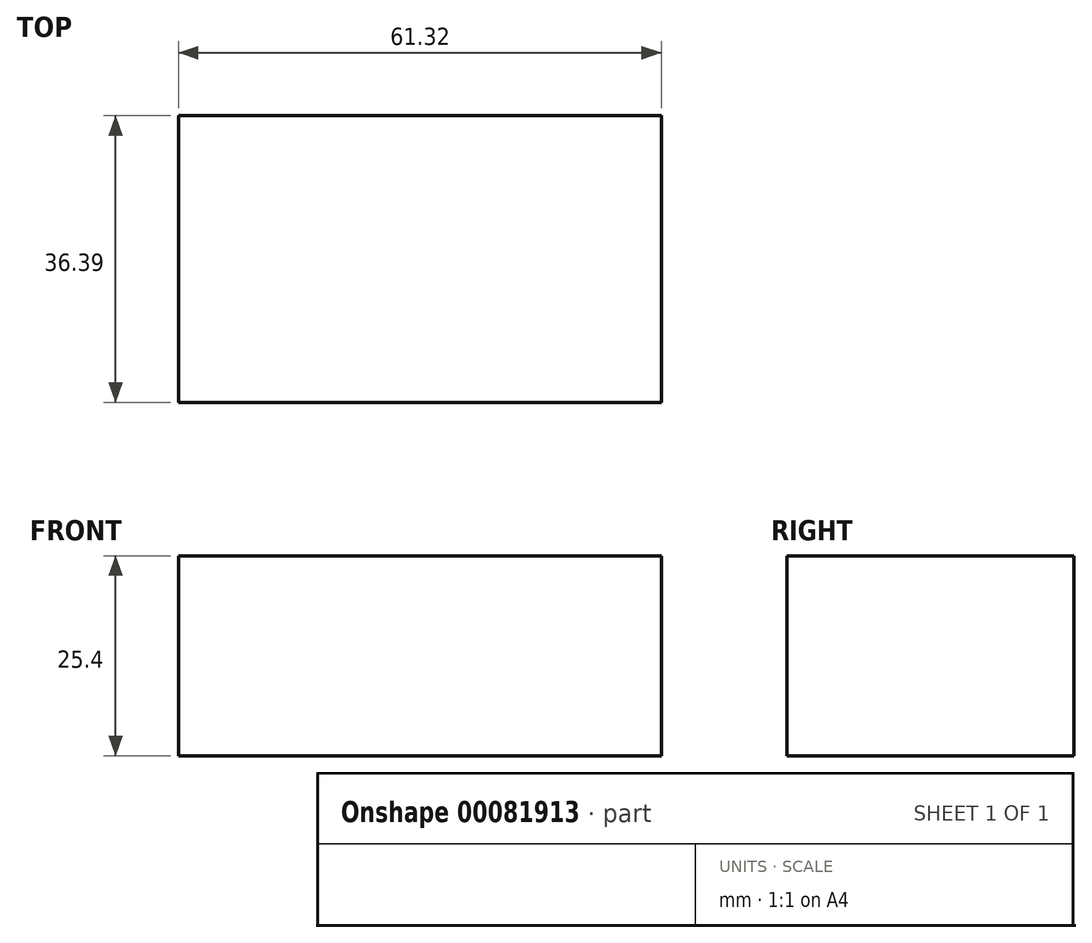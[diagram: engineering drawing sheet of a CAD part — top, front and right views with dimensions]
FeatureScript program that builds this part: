
annotation { "Feature Type Name" : "Feature", "Feature Type Description" : "" }
export const myFeature = defineFeature(function(context is Context, id is Id, definition is map)
    precondition{}
    {
        {
            var Q0;
            Q0=qCreatedBy(makeId("Top.planeOp"),FACE);
            var sketch = newSketch(context, id + "F0", { "sketchPlane" : qUnion([Q0])});
            skLineSegment(sketch, "E0.bottom", {"start": v(-191.71, 39.69) * mm, "end": v(-130.39, 39.69) * mm});
            skLineSegment(sketch, "E0.top", {"start": v(-191.71, 3.3) * mm, "end": v(-130.39, 3.3) * mm});
            skLineSegment(sketch, "E0.left", {"start": v(-191.71, 39.69) * mm, "end": v(-191.71, 3.3) * mm});
            skLineSegment(sketch, "E0.right", {"start": v(-130.39, 39.69) * mm, "end": v(-130.39, 3.3) * mm});
            skSolve(sketch);
        }
        {
            var Q0;
            Q0 = qSketchRegion(id + "F0", true);
            extrude(context, id + "F1", {"entities" : qUnion([Q0]), "depth" : 25.4 * mm});
        }
    });
